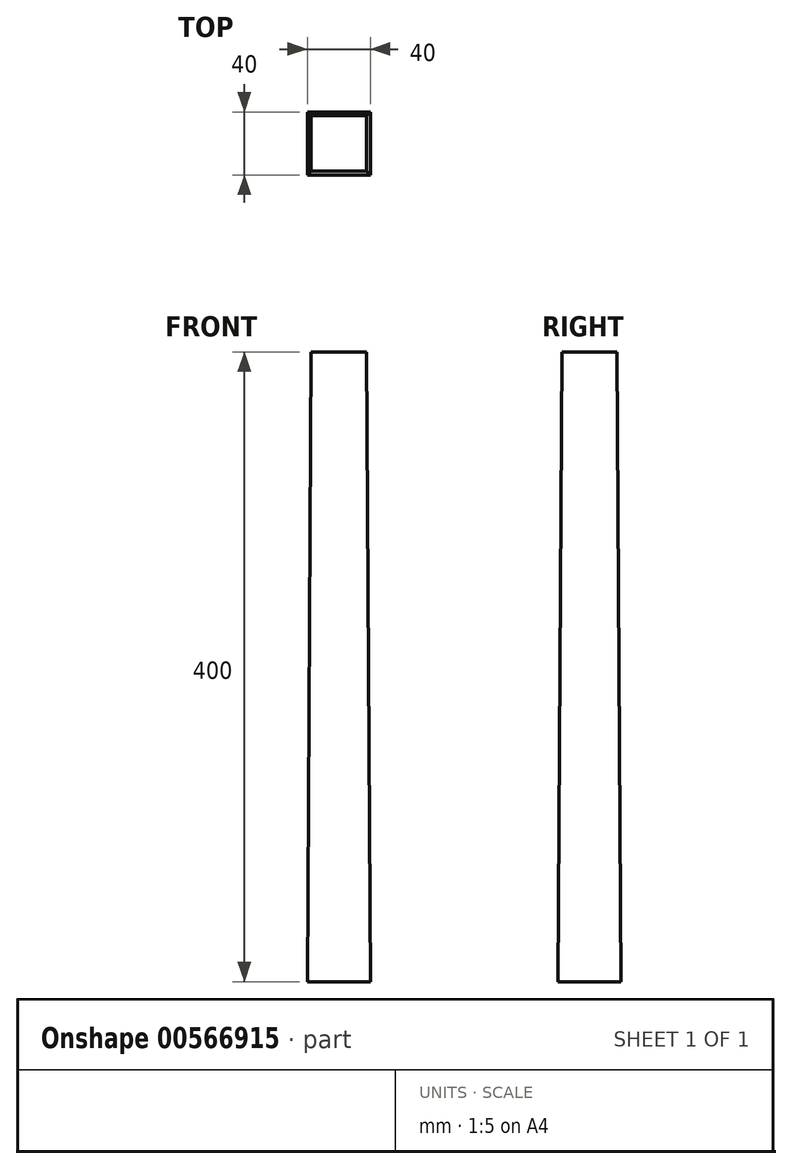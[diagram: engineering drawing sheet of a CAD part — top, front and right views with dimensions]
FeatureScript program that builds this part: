
annotation { "Feature Type Name" : "Feature", "Feature Type Description" : "" }
export const myFeature = defineFeature(function(context is Context, id is Id, definition is map)
    precondition{}
    {
        {
            var Q0;
            Q0=qCreatedBy(makeId("Top.planeOp"),FACE);
            var sketch = newSketch(context, id + "F0", { "sketchPlane" : qUnion([Q0])});
            skLineSegment(sketch, "E0.bottom", {"start": v(20, 20) * mm, "end": v(-20, 20) * mm});
            skLineSegment(sketch, "E0.top", {"start": v(20, -20) * mm, "end": v(-20, -20) * mm});
            skLineSegment(sketch, "E0.left", {"start": v(20, 20) * mm, "end": v(20, -20) * mm});
            skLineSegment(sketch, "E0.right", {"start": v(-20, 20) * mm, "end": v(-20, -20) * mm});
            skPoint(sketch, "E0.middle", {"position": v(0, 0) * mm});
            skSolve(sketch);
        }
        {
            var Q0;
            Q0=qCreatedBy(makeId("Top.planeOp"),FACE);
            cPlane(context, id + "F1", {"entities" : qUnion([Q0]), "cplaneType" : CPlaneType.OFFSET, "offset" : 400 * mm, "width" : 150 * mm, "height" : 150 * mm});
        }
        {
            var Q0;
            Q0=qCreatedBy(id+"F1.planeOp",FACE);
            var sketch = newSketch(context, id + "F2", { "sketchPlane" : qUnion([Q0])});
            skLineSegment(sketch, "E1.bottom", {"start": v(-17.5, 17.5) * mm, "end": v(17.5, 17.5) * mm});
            skLineSegment(sketch, "E1.top", {"start": v(-17.5, -17.5) * mm, "end": v(17.5, -17.5) * mm});
            skLineSegment(sketch, "E1.left", {"start": v(-17.5, 17.5) * mm, "end": v(-17.5, -17.5) * mm});
            skLineSegment(sketch, "E1.right", {"start": v(17.5, 17.5) * mm, "end": v(17.5, -17.5) * mm});
            skPoint(sketch, "E1.middle", {"position": v(0, 0) * mm});
            skSolve(sketch);
        }
        {
            var Q0;
            Q0 = qSketchRegion(id + "F2", true);
            var Q1;
            Q1 = qSketchRegion(id + "F0", true);
            loft(context, id + "F3", {"sheetProfilesArray" : [{ "sheetProfileEntities" : qUnion([Q0]) }, { "sheetProfileEntities" : qUnion([Q1]) }]});
        }
    });
